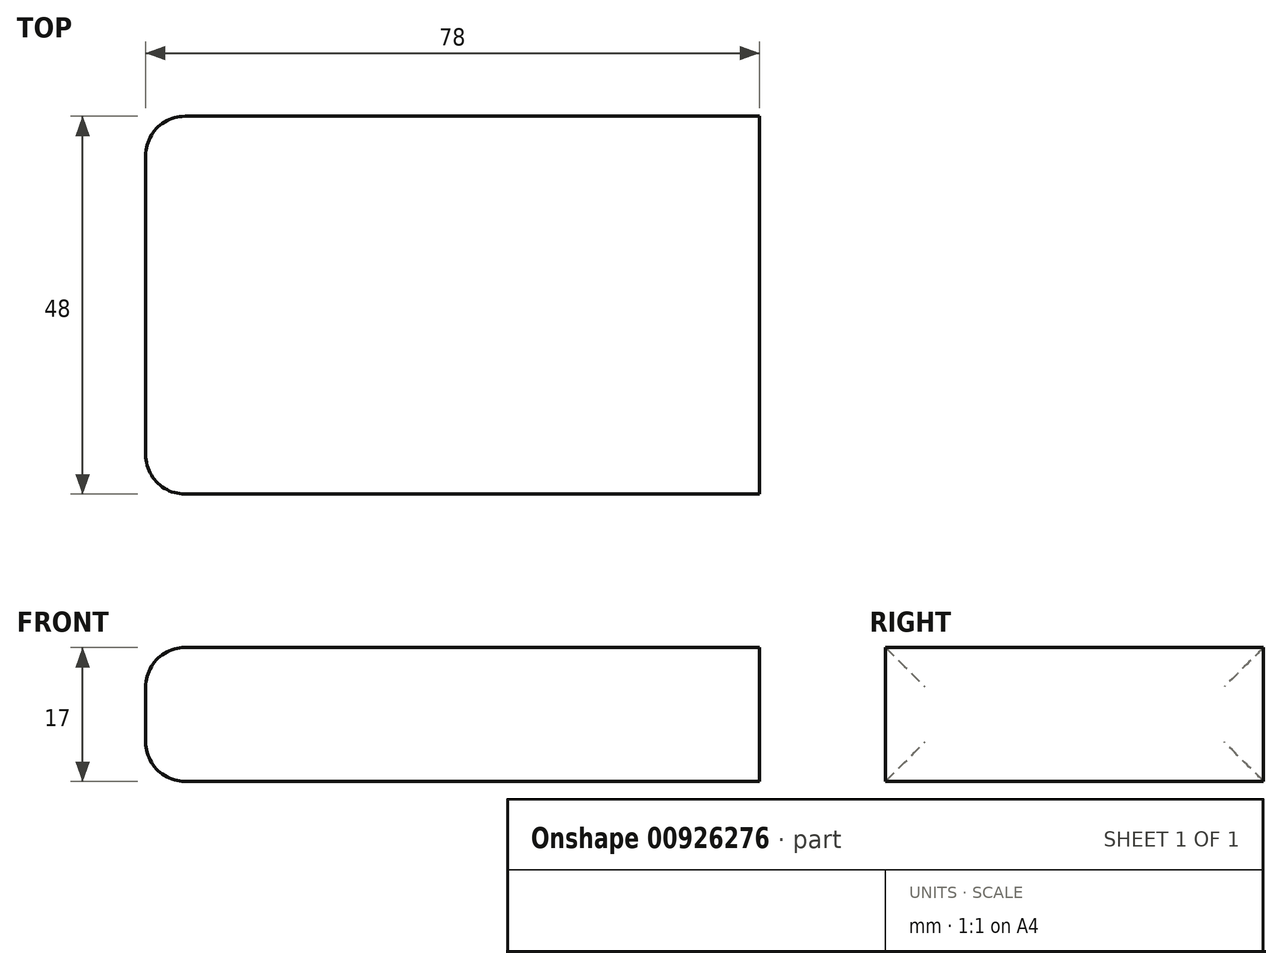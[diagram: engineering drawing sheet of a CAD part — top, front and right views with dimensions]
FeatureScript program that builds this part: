
annotation { "Feature Type Name" : "Feature", "Feature Type Description" : "" }
export const myFeature = defineFeature(function(context is Context, id is Id, definition is map)
    precondition{}
    {
        {
            var Q0;
            Q0=qCreatedBy(makeId("Top.planeOp"),FACE);
            var sketch = newSketch(context, id + "F0", { "sketchPlane" : qUnion([Q0])});
            skLineSegment(sketch, "E0.bottom", {"start": v(-31.83, 21.85) * mm, "end": v(46.17, 21.85) * mm});
            skLineSegment(sketch, "E0.top", {"start": v(-31.83, -26.15) * mm, "end": v(46.17, -26.15) * mm});
            skLineSegment(sketch, "E0.left", {"start": v(-31.83, 21.85) * mm, "end": v(-31.83, -26.15) * mm});
            skLineSegment(sketch, "E0.right", {"start": v(46.17, 21.85) * mm, "end": v(46.17, -26.15) * mm});
            skSolve(sketch);
        }
        {
            var Q0;
            Q0=makeQuery(id+"F0.imprint","IMPRINT",FACE,{"disambiguationData":[TD([[makeQuery(id+"F0.imprint","IMPRINT",EDGE,{"derivedFrom":sQuery(id+"F0.wireOp",EDGE,"E0.bottom")}),-1.0]])]});
            extrude(context, id + "F1", {"entities" : qUnion([Q0]), "depth" : 17 * mm, "offsetDistance" : 25 * mm});
        }
        {
            var Q0;
            Q0=makeQuery(id+"F1.opExtrude","SWEPT_FACE",FACE,{"disambiguationData":[OSD([sQuery(id+"F0.wireOp",EDGE,"E0.left")])]});
            fillet(context, id + "F2", {"entities" : qUnion([Q0]), "radius" : 5 * mm, "allowEdgeOverflow" : false});
        }
    });
